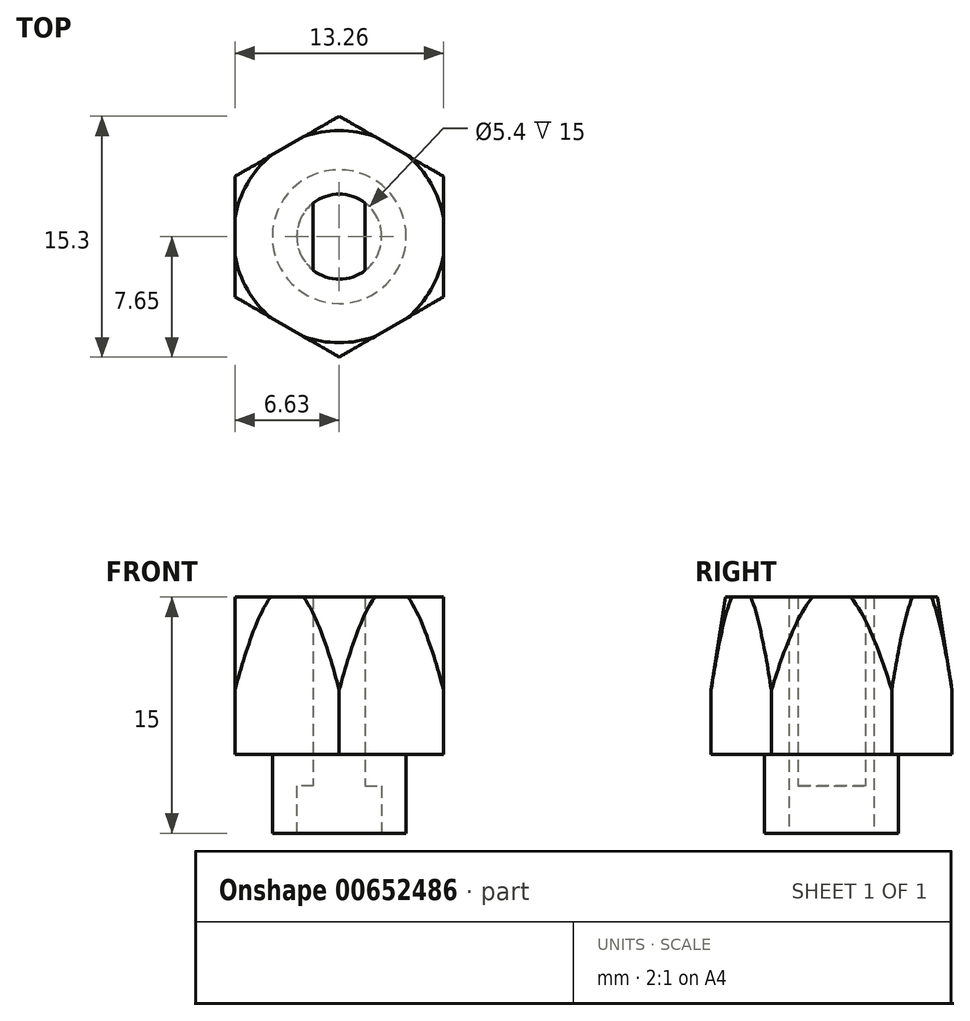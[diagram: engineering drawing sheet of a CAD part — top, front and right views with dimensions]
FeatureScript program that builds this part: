
annotation { "Feature Type Name" : "Feature", "Feature Type Description" : "" }
export const myFeature = defineFeature(function(context is Context, id is Id, definition is map)
    precondition{}
    {
        {
            var Q0;
            Q0=qCreatedBy(makeId("Top.planeOp"),FACE);
            var sketch = newSketch(context, id + "F0", { "sketchPlane" : qUnion([Q0])});
            skCircle(sketch, "E0", {"center": v(0, 0) * mm, "radius": 2.7 * mm});
            skLineSegment(sketch, "E1", {"start": v(-1.65, -2.14) * mm, "end": v(-1.65, 2.14) * mm});
            skLineSegment(sketch, "E2", {"start": v(1.65, 2.14) * mm, "end": v(1.65, -2.14) * mm});
            skCircle(sketch, "E3.cCircle", {"center": v(0, 0) * mm, "radius": 7.65 * mm, "construction": true});
            skLineSegment(sketch, "E3.0", {"start": v(0, -7.65) * mm, "end": v(-6.63, -3.83) * mm});
            skLineSegment(sketch, "E3.1", {"start": v(-6.63, -3.83) * mm, "end": v(-6.63, 3.82) * mm});
            skLineSegment(sketch, "E3.2", {"start": v(-6.63, 3.82) * mm, "end": v(0, 7.65) * mm});
            skLineSegment(sketch, "E3.3", {"start": v(0, 7.65) * mm, "end": v(6.63, 3.83) * mm});
            skLineSegment(sketch, "E3.4", {"start": v(6.63, 3.83) * mm, "end": v(6.63, -3.83) * mm});
            skLineSegment(sketch, "E3.5", {"start": v(6.63, -3.82) * mm, "end": v(0, -7.65) * mm});
            skCircle(sketch, "E4", {"center": v(0, 0) * mm, "radius": 4.25 * mm});
            skSolve(sketch);
        }
        {
            var Q0;
            Q0=makeQuery(id+"F0.imprint","IMPRINT",FACE,{"disambiguationData":[TD([[makeQuery(id+"F0.imprint","IMPRINT",EDGE,{"derivedFrom":sQuery(id+"F0.wireOp",EDGE,"E4")}),1.0]])]});
            extrude(context, id + "F1", {"entities" : qUnion([Q0]), "depth" : 3 * mm, "offsetDistance" : 25 * mm});
        }
        {
            var Q0;
            {var subQ0=sQuery(id+"F0.wireOp",EDGE,"E1");Q0=makeQuery(id+"F0.imprint","IMPRINT",FACE,{"disambiguationData":[TD([[makeQuery(id+"F0.imprint","IMPRINT",EDGE,{"derivedFrom":subQ0}),1.0]])]});}
            var Q1;
            {var subQ0=sQuery(id+"F0.wireOp",EDGE,"E2");Q1=makeQuery(id+"F0.imprint","IMPRINT",FACE,{"disambiguationData":[TD([[makeQuery(id+"F0.imprint","IMPRINT",EDGE,{"derivedFrom":subQ0}),1.0]])]});}
            var Q2;
            Q2=makeQuery(id+"F0.imprint","IMPRINT",FACE,{"disambiguationData":[TD([[makeQuery(id+"F0.imprint","IMPRINT",EDGE,{"derivedFrom":sQuery(id+"F0.wireOp",EDGE,"E4")}),1.0]])]});
            var Q3;
            Q3=makeQuery(id+"F1.opExtrude","CAP_FACE",FACE,{"disambiguationData":[OSD([sQuery(id+"F0.wireOp",EDGE,"E0"),sQuery(id+"F0.wireOp",EDGE,"E4")])],"isStart":false});
            var Q4;
            Q4=makeQuery(id+"F1.opExtrude","CAP_FACE",FACE,{"disambiguationData":[OSD([sQuery(id+"F0.wireOp",EDGE,"E0"),sQuery(id+"F0.wireOp",EDGE,"E4")])],"isStart":false});
            extrude(context, id + "F2", {"entities" : qUnion([Q0, Q1, Q2]), "operationType" : NewBodyOperationType.ADD, "endBound" : BoundingType.UP_TO_SURFACE, "depth" : 25 * mm, "endBoundEntityFace" : qUnion([Q3]), "hasOffset" : true, "offsetDistance" : 2 * mm, "offsetOppositeDirection" : true, "hasSecondDirection" : true, "secondDirectionBound" : SecondDirectionBoundingType.UP_TO_SURFACE, "secondDirectionOppositeDirection" : false, "secondDirectionDepth" : 25 * mm, "secondDirectionBoundEntityFace" : qUnion([Q4])});
        }
        {
            var Q0;
            Q0=makeQuery(id+"F0.imprint","IMPRINT",FACE,{"disambiguationData":[TD([[makeQuery(id+"F0.imprint","IMPRINT",EDGE,{"derivedFrom":sQuery(id+"F0.wireOp",EDGE,"E3.0")}),-1.0]])]});
            var Q1;
            Q1=makeQuery(id+"F0.imprint","IMPRINT",FACE,{"disambiguationData":[TD([[makeQuery(id+"F0.imprint","IMPRINT",EDGE,{"derivedFrom":sQuery(id+"F0.wireOp",EDGE,"E4")}),1.0]])]});
            var Q2;
            {var subQ0=sQuery(id+"F0.wireOp",EDGE,"E2");Q2=makeQuery(id+"F0.imprint","IMPRINT",FACE,{"disambiguationData":[TD([[makeQuery(id+"F0.imprint","IMPRINT",EDGE,{"derivedFrom":subQ0}),1.0]])]});}
            var Q3;
            {var subQ0=sQuery(id+"F0.wireOp",EDGE,"E1");Q3=makeQuery(id+"F0.imprint","IMPRINT",FACE,{"disambiguationData":[TD([[makeQuery(id+"F0.imprint","IMPRINT",EDGE,{"derivedFrom":subQ0}),1.0]])]});}
            var Q4;
            Q4=makeQuery(id+"F2.opExtrude","CAP_FACE",FACE,{"disambiguationData":[OSD([sQuery(id+"F0.wireOp",EDGE,"E0"),sQuery(id+"F0.wireOp",EDGE,"E4")])],"isStart":false});
            var Q5;
            Q5=makeQuery(id+"F2.opExtrude","CAP_FACE",FACE,{"disambiguationData":[OSD([sQuery(id+"F0.wireOp",EDGE,"E0"),sQuery(id+"F0.wireOp",EDGE,"E4")])],"isStart":false});
            extrude(context, id + "F3", {"entities" : qUnion([Q0, Q1, Q2, Q3]), "operationType" : NewBodyOperationType.ADD, "endBound" : BoundingType.UP_TO_SURFACE, "depth" : 25 * mm, "endBoundEntityFace" : qUnion([Q4]), "hasOffset" : true, "offsetDistance" : 10 * mm, "offsetOppositeDirection" : true, "hasSecondDirection" : true, "secondDirectionBound" : SecondDirectionBoundingType.UP_TO_SURFACE, "secondDirectionOppositeDirection" : false, "secondDirectionDepth" : 25 * mm, "secondDirectionBoundEntityFace" : qUnion([Q5])});
        }
        {
            var Q0;
            Q0=qCreatedBy(makeId("Right.planeOp"),FACE);
            var sketch = newSketch(context, id + "F4", { "sketchPlane" : qUnion([Q0])});
            skLineSegment(sketch, "E5", {"start": v(-6.6, 15.91) * mm, "end": v(-8.32, 4.82) * mm});
            skLineSegment(sketch, "E6", {"start": v(-8.32, 4.82) * mm, "end": v(-8.32, 15.91) * mm});
            skLineSegment(sketch, "E7", {"start": v(-8.32, 15.91) * mm, "end": v(-6.6, 15.91) * mm});
            skLineSegment(sketch, "E8", {"start": v(0, 0) * mm, "end": v(0, 9.84) * mm});
            skSolve(sketch);
        }
        {
            var Q0;
            Q0 = qSketchRegion(id + "F4", true);
            var Q1;
            Q1=sQuery(id+"F4.wireOp",EDGE,"E8");
            revolve(context, id + "F5", {"operationType" : NewBodyOperationType.REMOVE, "entities" : qUnion([Q0]), "axis" : qUnion([Q1]), "revolveType" : RevolveType.FULL, "oppositeDirection" : true, "surfaceOperationType" : NewSurfaceOperationType.NEW});
        }
    });
